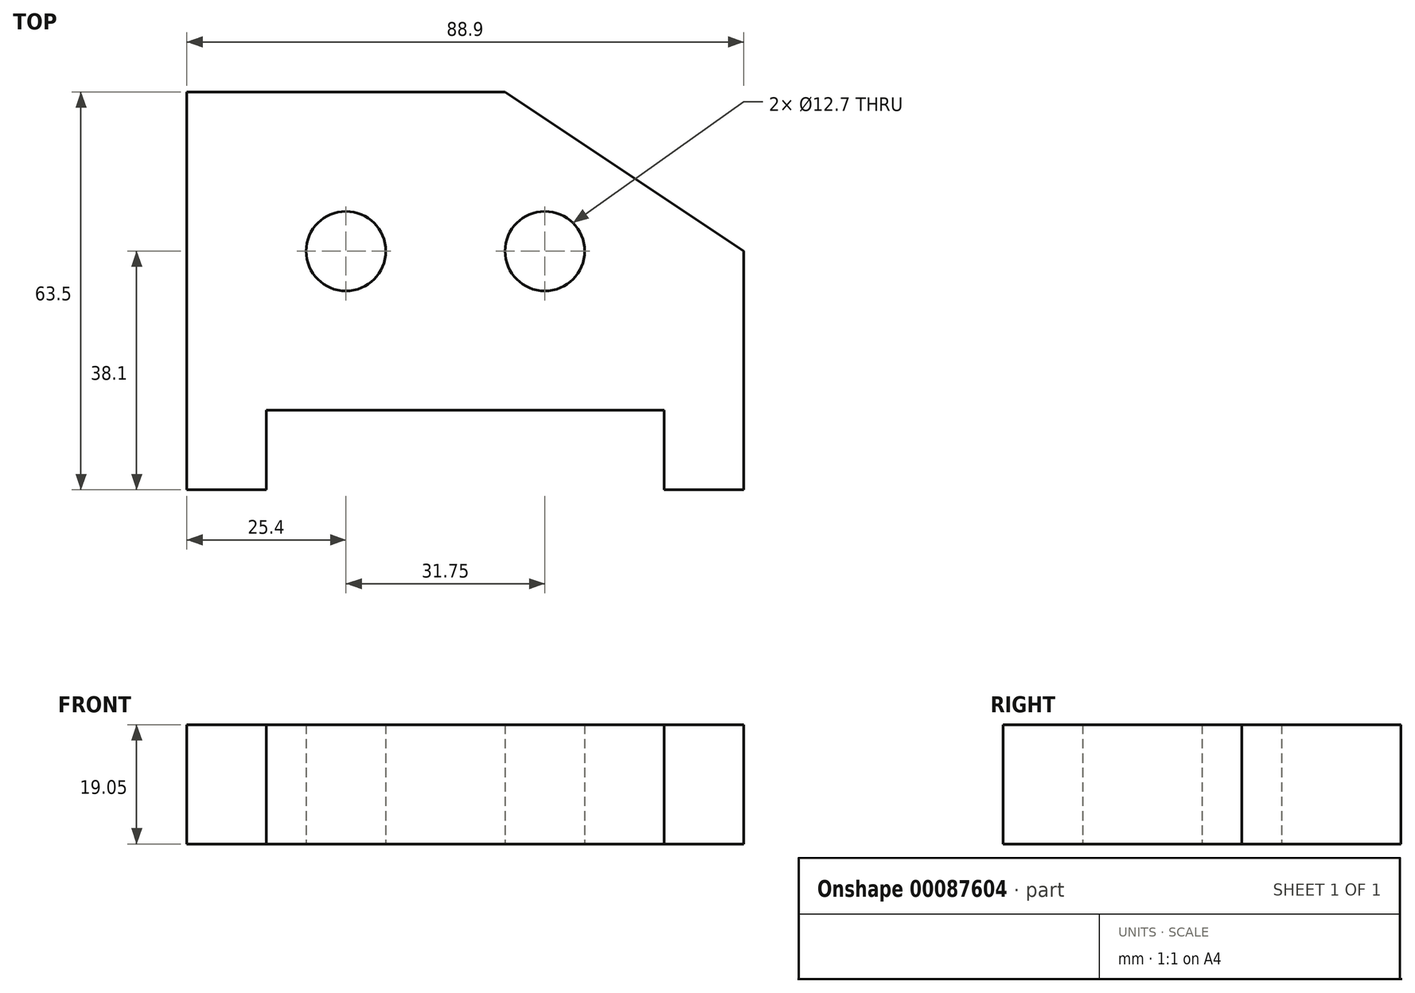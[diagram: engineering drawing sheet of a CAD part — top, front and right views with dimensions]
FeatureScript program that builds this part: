
annotation { "Feature Type Name" : "Feature", "Feature Type Description" : "" }
export const myFeature = defineFeature(function(context is Context, id is Id, definition is map)
    precondition{}
    {
        {
            var Q0;
            Q0=qCreatedBy(makeId("Top.planeOp"),FACE);
            var sketch = newSketch(context, id + "F0", { "sketchPlane" : qUnion([Q0])});
            skLineSegment(sketch, "E0.bottom", {"start": v(0, 0) * mm, "end": v(12.7, 0) * mm});
            skLineSegment(sketch, "E0.top", {"start": v(0, 63.5) * mm, "end": v(50.8, 63.5) * mm});
            skLineSegment(sketch, "E0.left", {"start": v(0, 0) * mm, "end": v(0, 63.5) * mm});
            skLineSegment(sketch, "E0.right", {"start": v(88.9, 0) * mm, "end": v(88.9, 38.1) * mm});
            skLineSegment(sketch, "E1.top", {"start": v(12.7, 12.7) * mm, "end": v(76.2, 12.7) * mm});
            skLineSegment(sketch, "E1.left", {"start": v(12.7, 0) * mm, "end": v(12.7, 12.7) * mm});
            skLineSegment(sketch, "E1.right", {"start": v(76.2, 0) * mm, "end": v(76.2, 12.7) * mm});
            skLineSegment(sketch, "E2", {"start": v(88.9, 38.1) * mm, "end": v(50.8, 63.5) * mm});
            skCircle(sketch, "E3", {"center": v(25.4, 38.1) * mm, "radius": 6.35 * mm});
            skCircle(sketch, "E4", {"center": v(57.15, 38.1) * mm, "radius": 6.35 * mm});
            skLineSegment(sketch, "E5", {"start": v(57.15, 38.1) * mm, "end": v(25.4, 38.1) * mm, "construction": true});
            skLineSegment(sketch, "E6.trimOffspring", {"start": v(76.2, 0) * mm, "end": v(88.9, 0) * mm});
            skSolve(sketch);
        }
        {
            var Q0;
            Q0 = qSketchRegion(id + "F0", true);
            extrude(context, id + "F1", {"entities" : qUnion([Q0]), "depth" : 19.05 * mm});
        }
    });
